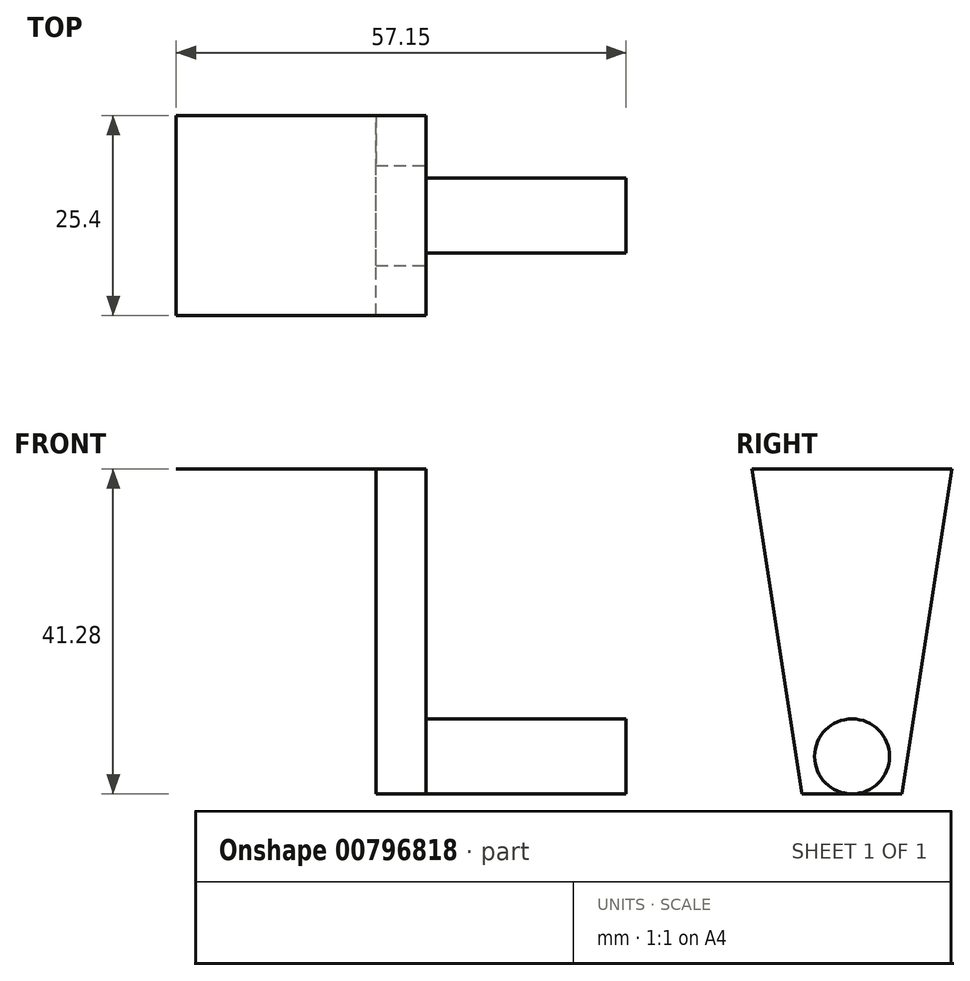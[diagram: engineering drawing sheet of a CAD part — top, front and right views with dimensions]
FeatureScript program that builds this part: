
annotation { "Feature Type Name" : "Feature", "Feature Type Description" : "" }
export const myFeature = defineFeature(function(context is Context, id is Id, definition is map)
    precondition{}
    {
        {
            var Q0;
            Q0=qCreatedBy(makeId("Top.planeOp"),FACE);
            var sketch = newSketch(context, id + "F0", { "sketchPlane" : qUnion([Q0])});
            skLineSegment(sketch, "E0.bottom", {"start": v(-31.75, 12.7) * mm, "end": v(0, 12.7) * mm});
            skLineSegment(sketch, "E0.top", {"start": v(-31.75, -12.7) * mm, "end": v(0, -12.7) * mm});
            skLineSegment(sketch, "E0.left", {"start": v(-31.75, 12.7) * mm, "end": v(-31.75, -12.7) * mm});
            skLineSegment(sketch, "E0.right", {"start": v(0, 12.7) * mm, "end": v(0, -12.7) * mm});
            skSolve(sketch);
        }
        {
            var Q0;
            Q0=qCreatedBy(makeId("Right.planeOp"),FACE);
            var sketch = newSketch(context, id + "F1", { "sketchPlane" : qUnion([Q0])});
            skLineSegment(sketch, "E1.bottom", {"start": v(-12.7, 0) * mm, "end": v(12.7, 0) * mm});
            skCircle(sketch, "E2", {"center": v(0, -36.51) * mm, "radius": 4.76 * mm});
            skLineSegment(sketch, "E3", {"start": v(-12.7, 0) * mm, "end": v(-6.35, -41.28) * mm});
            skLineSegment(sketch, "E4", {"start": v(12.7, 0) * mm, "end": v(6.35, -41.28) * mm});
            skLineSegment(sketch, "E5", {"start": v(-6.35, -41.28) * mm, "end": v(6.35, -41.28) * mm});
            skLineSegment(sketch, "E6", {"start": v(0, -36.51) * mm, "end": v(0, -41.28) * mm, "construction": true});
            skSolve(sketch);
        }
        {
            var Q0;
            Q0=makeQuery(id+"F0.imprint","IMPRINT",FACE,{"disambiguationData":[TD([[makeQuery(id+"F0.imprint","IMPRINT",EDGE,{"derivedFrom":sQuery(id+"F0.wireOp",EDGE,"E0.bottom")}),-1.0]])]});
            extrude(context, id + "F2", {"entities" : qUnion([Q0]), "depth" : 1 / 203.2 * mm, "offsetDistance" : 25.4 * mm});
        }
        {
            var Q0;
            Q0=makeQuery(id+"F1.imprint","IMPRINT",FACE,{"disambiguationData":[TD([[makeQuery(id+"F1.imprint","IMPRINT",EDGE,{"derivedFrom":sQuery(id+"F1.wireOp",EDGE,"JqCqs5jJ-SMC5-ap2F-kZOG-SR7jAbwiLL7q")}),1.0]])]});
            var Q1;
            Q1=makeQuery(id+"F1.imprint","IMPRINT",FACE,{"disambiguationData":[TD([[makeQuery(id+"F1.imprint","IMPRINT",EDGE,{"derivedFrom":sQuery(id+"F1.wireOp",EDGE,"E1.bottom")}),-1.0]])]});
            var Q2;
            Q2=makeQuery(id+"F1.imprint","IMPRINT",FACE,{"disambiguationData":[TD([[makeQuery(id+"F1.imprint","IMPRINT",EDGE,{"derivedFrom":sQuery(id+"F1.wireOp",EDGE,"E2")}),1.0]])]});
            extrude(context, id + "F3", {"entities" : qUnion([Q0, Q1, Q2]), "operationType" : NewBodyOperationType.ADD, "oppositeDirection" : true, "depth" : 6.35 * mm, "offsetDistance" : 25.4 * mm});
        }
        {
            var Q0;
            Q0=makeQuery(id+"F1.imprint","IMPRINT",FACE,{"disambiguationData":[TD([[makeQuery(id+"F1.imprint","IMPRINT",EDGE,{"derivedFrom":sQuery(id+"F1.wireOp",EDGE,"E2")}),1.0]])]});
            extrude(context, id + "F4", {"entities" : qUnion([Q0]), "depth" : 25.4 * mm, "offsetDistance" : 25.4 * mm});
        }
    });
